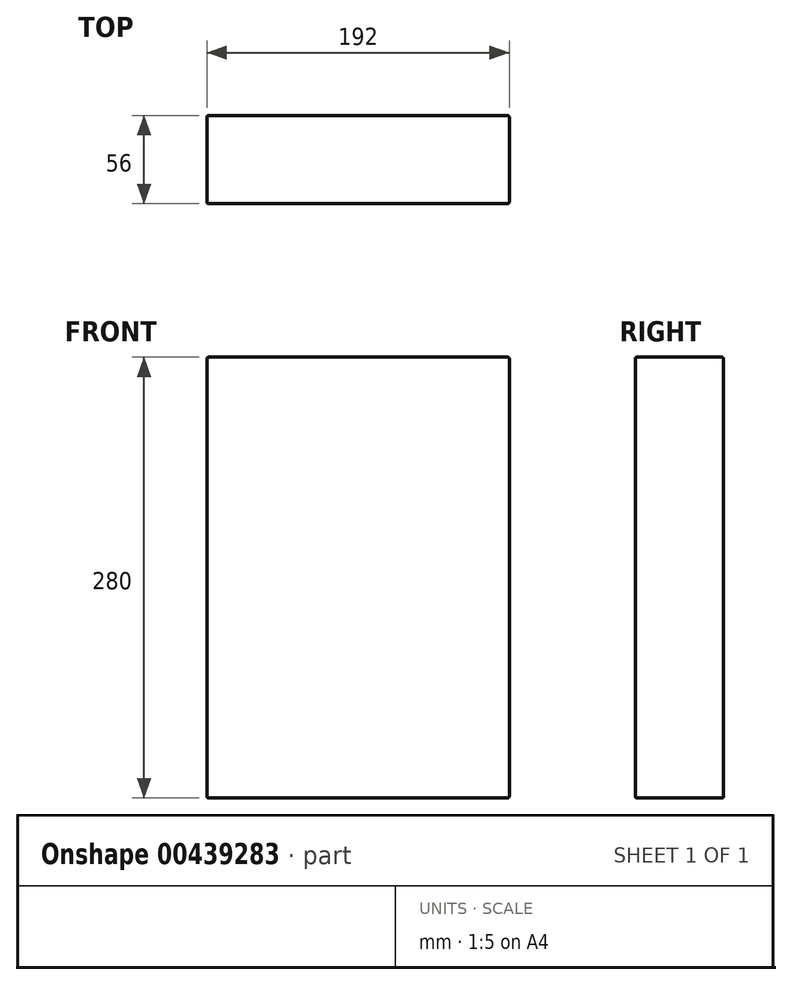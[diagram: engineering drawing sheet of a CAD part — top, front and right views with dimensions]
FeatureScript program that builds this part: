
annotation { "Feature Type Name" : "Feature", "Feature Type Description" : "" }
export const myFeature = defineFeature(function(context is Context, id is Id, definition is map)
    precondition{}
    {
        {
            var Q0;
            Q0=qCreatedBy(makeId("Top.planeOp"),FACE);
            var sketch = newSketch(context, id + "F0", { "sketchPlane" : qUnion([Q0])});
            skLineSegment(sketch, "E0.bottom", {"start": v(96, 28) * mm, "end": v(-96, 28) * mm});
            skLineSegment(sketch, "E0.top", {"start": v(96, -28) * mm, "end": v(-96, -28) * mm});
            skLineSegment(sketch, "E0.left", {"start": v(96, 28) * mm, "end": v(96, -28) * mm});
            skLineSegment(sketch, "E0.right", {"start": v(-96, 28) * mm, "end": v(-96, -28) * mm});
            skPoint(sketch, "E0.middle", {"position": v(0, 0) * mm});
            skSolve(sketch);
        }
        {
            var Q0;
            Q0 = qSketchRegion(id + "F0", true);
            extrude(context, id + "F1", {"entities" : qUnion([Q0]), "depth" : 280 * mm});
        }
        {
            var Q0;
            Q0=makeQuery(id+"F1.opExtrude","SWEPT_FACE",FACE,{"disambiguationData":[OSD([sQuery(id+"F0.wireOp",EDGE,"E0.top")])]});
            var Q1;
            Q1=makeQuery(id+"F1.opExtrude","CAP_FACE",FACE,{"disambiguationData":[OSD([sQuery(id+"F0.wireOp",EDGE,"E0.bottom"),sQuery(id+"F0.wireOp",EDGE,"E0.top"),sQuery(id+"F0.wireOp",EDGE,"E0.left"),sQuery(id+"F0.wireOp",EDGE,"E0.right")])],"isStart":false});
            var Q2;
            Q2=makeQuery(id+"F1.opExtrude","SWEPT_FACE",FACE,{"disambiguationData":[OSD([sQuery(id+"F0.wireOp",EDGE,"E0.right")])]});
            var Q3;
            Q3=makeQuery(id+"F1.opExtrude","SWEPT_FACE",FACE,{"disambiguationData":[OSD([sQuery(id+"F0.wireOp",EDGE,"E0.left")])]});
            var Q4;
            Q4=makeQuery(id+"F1.opExtrude","SWEPT_FACE",FACE,{"disambiguationData":[OSD([sQuery(id+"F0.wireOp",EDGE,"E0.bottom")])]});
            var Q5;
            Q5=makeQuery(id+"F1.opExtrude","CAP_FACE",FACE,{"disambiguationData":[OSD([sQuery(id+"F0.wireOp",EDGE,"E0.bottom"),sQuery(id+"F0.wireOp",EDGE,"E0.top"),sQuery(id+"F0.wireOp",EDGE,"E0.left"),sQuery(id+"F0.wireOp",EDGE,"E0.right")])],"isStart":true});
            fillet(context, id + "F2", {"entities" : qUnion([Q0, Q1, Q2, Q3, Q4, Q5]), "radius" : 1 * mm, "tangentPropagation" : true, "allowEdgeOverflow" : false});
        }
    });
